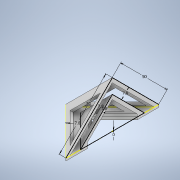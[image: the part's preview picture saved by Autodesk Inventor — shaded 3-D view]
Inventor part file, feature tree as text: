
AUTODESK INVENTOR PART (.ipt)
format: ipt  version: 2020 (Build 240168000, 168)  size: 241,664 bytes
history: native  units: mm
features: extrude x10, sketch x10, plane x4, split x2, shell x2
ambient origin geometry x8: Origin, YZ Plane, XZ Plane, XY Plane, X Axis, Y Axis, Z Axis, Center Point
bodies: Solid1 (feature_tree), Solid4 (feature_tree)
feature tree (28):
  extrude  "Extrusion1"  Depth=2.0mm TaperAngle=0.0deg
  sketch  "Sketch3"  dims[d1=50.0mm d2=2.0mm d3=0.0mm]
  sketch  "Sketch12"  dims[d41=70.71mm d42=50.0mm d43=50.0mm]
  plane  "Work Plane5"
  plane  "Work Plane6"
  extrude  "Extrusion10"  Depth=50.0mm
  split  "Split3"
  shell  "Shell3"  Thickness=50.0mm
  sketch  "Sketch13"  dims[d44=10.0mm d45=0.0mm d46=0.0mm d47=7.8mm]
  plane  "Work Plane9"
  plane  "Work Plane10"
  extrude  "Extrusion18"  TaperAngle=0.0deg  [1 undecoded]
  split  "Split5"
  shell  "Shell5"  Thickness=7.8mm
  extrude  "Extrusion19"  Depth=2.0mm
  extrude  "Extrusion20"  Depth=7.8mm
  extrude  "Extrusion21"  Depth=2.0mm
  extrude  "Extrusion22"  Depth=4.0mm
  extrude  "Extrusion23"  Depth=4.0mm
  extrude  "Extrusion24"  Depth=2.0mm
  extrude  "Extrusion25"  Depth=2.0mm
  sketch  "Sketch20"  dims[d48=7.8mm d49=2.0mm]
  sketch  "Sketch21"  dims[d52=7.8mm d53=7.8mm]
  sketch  "Sketch22"  dims[d85=10.0mm d86=0.0mm d87=2.0mm]
  sketch  "Sketch23"  dims[d88=10.0mm d89=0.0mm d90=4.0mm]
  sketch  "Sketch24"  dims[d91=4.0mm d92=4.0mm]
  sketch  "Sketch25"  dims[d93=2.0mm d94=0.0mm d95=4.0mm]
  sketch  "Sketch27"  dims[d96=4.0mm d97=4.0mm d98=2.0mm d99=0.0mm d100=7.0mm d101=4.0mm d102=4.0mm d103=2.0mm d104=0.0mm d105=7.0mm d106=4.0mm d107=4.0mm d108=2.0mm d109=0.0mm d110=2.0mm d111=0.0mm d112=2.0mm d113=0.0mm d114=0.5mm d115=0.872665mm]
note: 1 required parameter value undecoded (feature->parameter linkage not recoverable at this tier; creation-order binding heuristic only, values carry confidence <= 0.55)
